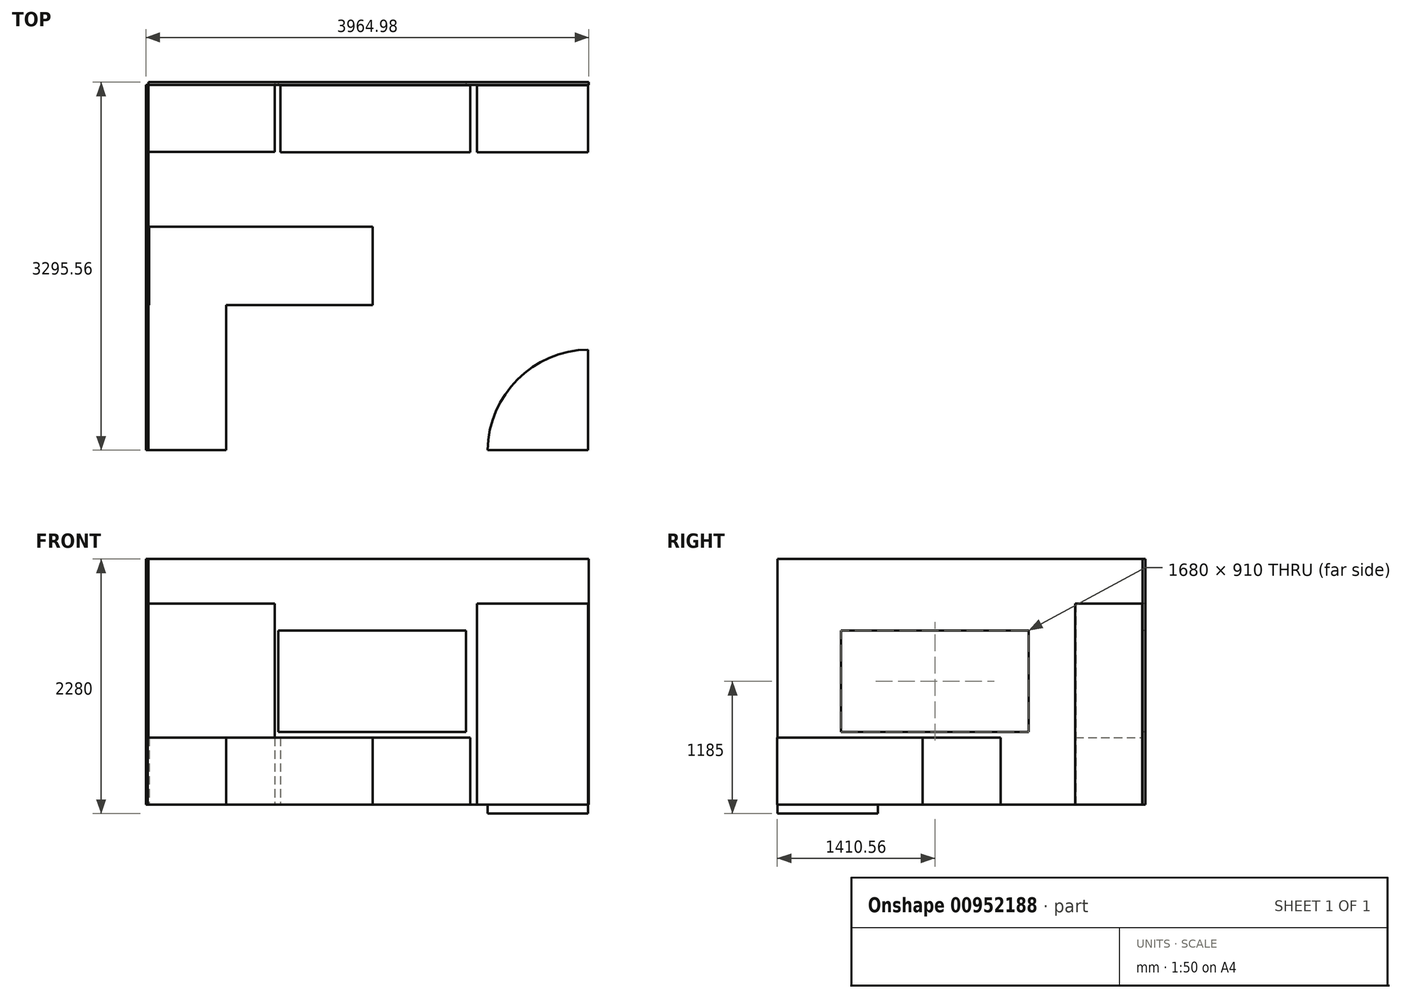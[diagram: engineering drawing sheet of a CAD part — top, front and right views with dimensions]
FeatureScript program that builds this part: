
annotation { "Feature Type Name" : "Feature", "Feature Type Description" : "" }
export const myFeature = defineFeature(function(context is Context, id is Id, definition is map)
    precondition{}
    {
        {
            var Q0;
            Q0=qCreatedBy(makeId("Top.planeOp"),FACE);
            var sketch = newSketch(context, id + "F0", { "sketchPlane" : qUnion([Q0])});
            skLineSegment(sketch, "E0.bottom", {"start": v(-2865.65, 1719.63) * mm, "end": v(1074.35, 1719.63) * mm});
            skLineSegment(sketch, "E0.top", {"start": v(-2865.65, -1550.37) * mm, "end": v(1074.35, -1550.37) * mm});
            skLineSegment(sketch, "E0.left", {"start": v(-2865.65, 1719.63) * mm, "end": v(-2865.65, -1550.37) * mm});
            skLineSegment(sketch, "E0.right", {"start": v(1074.35, 1719.63) * mm, "end": v(1074.35, -1550.37) * mm});
            skLineSegment(sketch, "E1", {"start": v(-2865.65, 699.63) * mm, "end": v(-2865.65, -980.37) * mm});
            skLineSegment(sketch, "E2", {"start": v(-1505.65, 1719.63) * mm, "end": v(174.35, 1719.63) * mm});
            skLineSegment(sketch, "E3", {"start": v(1070.5, -1539.26) * mm, "end": v(1074.35, -650.37) * mm});
            skLineSegment(sketch, "E4", {"start": v(1074.35, -650.37) * mm, "end": v(1074.35, -1550.37) * mm});
            skLineSegment(sketch, "E5", {"start": v(1074.35, -1550.37) * mm, "end": v(174.35, -1550.37) * mm});
            skArc(sketch, "E6", {"start": v(1074.35, -650.37) * mm, "mid": v(442.53, -918.55) * mm, "end": v(174.35, -1550.37) * mm});
            skSolve(sketch);
        }
        {
            var Q0;
            Q0=makeQuery(id+"F0.imprint","IMPRINT",FACE,{"disambiguationData":[TD([[makeQuery(id+"F0.imprint","IMPRINT",EDGE,{"derivedFrom":sQuery(id+"F0.wireOp",EDGE,"E0.bottom")}),-1.0]])]});
            var sketch = newSketch(context, id + "F1", { "sketchPlane" : qUnion([Q0])});
            skLineSegment(sketch, "E7.bottom", {"start": v(79.6, 1116.05) * mm, "end": v(1079.6, 1116.05) * mm});
            skLineSegment(sketch, "E7.top", {"start": v(79.6, 1716.05) * mm, "end": v(1079.6, 1716.05) * mm});
            skLineSegment(sketch, "E7.left", {"start": v(79.6, 1116.05) * mm, "end": v(79.6, 1716.05) * mm});
            skLineSegment(sketch, "E7.right", {"start": v(1079.6, 1116.05) * mm, "end": v(1079.6, 1716.05) * mm});
            skSolve(sketch);
        }
        {
            var Q0;
            Q0=makeQuery(id+"F0.imprint","IMPRINT",FACE,{"disambiguationData":[TD([[makeQuery(id+"F0.imprint","IMPRINT",EDGE,{"derivedFrom":sQuery(id+"F0.wireOp",EDGE,"E0.bottom")}),-1.0]])]});
            var sketch = newSketch(context, id + "F2", { "sketchPlane" : qUnion([Q0])});
            skLineSegment(sketch, "E8.bottom", {"start": v(-2858.85, 1719.76) * mm, "end": v(-1728.85, 1719.76) * mm});
            skLineSegment(sketch, "E8.top", {"start": v(-2858.85, 1119.76) * mm, "end": v(-1728.85, 1119.76) * mm});
            skLineSegment(sketch, "E8.left", {"start": v(-2858.85, 1719.76) * mm, "end": v(-2858.85, 1119.76) * mm});
            skLineSegment(sketch, "E8.right", {"start": v(-1728.85, 1719.76) * mm, "end": v(-1728.85, 1119.76) * mm});
            skSolve(sketch);
        }
        {
            var Q0;
            {var subQ0=sQuery(id+"F2.wireOp",EDGE,"E8.top");Q0=makeQuery(id+"F2.imprint","IMPRINT",FACE,{"disambiguationData":[TD([[makeQuery(id+"F2.imprint","IMPRINT",EDGE,{"derivedFrom":subQ0}),1.0]])]});}
            extrude(context, id + "F3", {"entities" : qUnion([Q0]), "depth" : 1800 * mm, "offsetDistance" : 25 * mm});
        }
        {
            var Q0;
            {var subQ0=sQuery(id+"F1.wireOp",EDGE,"E7.left");Q0=makeQuery(id+"F1.imprint","IMPRINT",FACE,{"disambiguationData":[TD([[makeQuery(id+"F1.imprint","IMPRINT",EDGE,{"derivedFrom":subQ0}),-1.0]])]});}
            extrude(context, id + "F4", {"entities" : qUnion([Q0]), "depth" : 1800 * mm, "offsetDistance" : 25 * mm});
        }
        {
            var Q0;
            {var subQ4=sQuery(id+"F0.wireOp",EDGE,"E0.top");Q0=makeQuery(id+"F0.imprint","IMPRINT",FACE,{"disambiguationData":[TD([[makeQuery(id+"F0.imprint","IMPRINT",EDGE,{"derivedFrom":subQ4}),1.0]])]});}
            var Q1;
            Q1=makeQuery(id+"F0.imprint","IMPRINT",FACE,{"disambiguationData":[TD([[makeQuery(id+"F0.imprint","IMPRINT",EDGE,{"derivedFrom":sQuery(id+"F0.wireOp",EDGE,"E4")}),-1.0]])]});
            extrude(context, id + "F5", {"entities" : qUnion([Q0, Q1]), "oppositeDirection" : true, "depth" : 80 * mm, "offsetDistance" : 25 * mm});
        }
        {
            var Q0;
            Q0=makeQuery(id+"F3.opExtrude","SWEPT_FACE",FACE,{"disambiguationData":[OSD([sQuery(id+"F0.wireOp",EDGE,"E0.bottom")])]});
            var sketch = newSketch(context, id + "F6", { "sketchPlane" : qUnion([Q0])});
            skLineSegment(sketch, "E9.bottom", {"start": v(18.85, 1560) * mm, "end": v(1698.85, 1560) * mm});
            skLineSegment(sketch, "E9.top", {"start": v(18.85, 650) * mm, "end": v(1698.85, 650) * mm});
            skLineSegment(sketch, "E9.left", {"start": v(18.85, 1560) * mm, "end": v(18.85, 650) * mm});
            skLineSegment(sketch, "E9.right", {"start": v(1698.85, 1560) * mm, "end": v(1698.85, 650) * mm});
            skLineSegment(sketch, "E10.bottom", {"start": v(2858.85, 0) * mm, "end": v(-1081.13, 0) * mm});
            skLineSegment(sketch, "E10.top", {"start": v(2858.85, 2200) * mm, "end": v(-1081.13, 2200) * mm});
            skLineSegment(sketch, "E10.left", {"start": v(2858.85, 0) * mm, "end": v(2858.85, 2200) * mm});
            skLineSegment(sketch, "E10.right", {"start": v(-1081.13, 0) * mm, "end": v(-1081.13, 2200) * mm});
            skLineSegment(sketch, "E11.bottom", {"start": v(190.6, 2200) * mm, "end": v(147.5, 2200) * mm});
            skSolve(sketch);
        }
        {
            var Q0;
            Q0=makeQuery(id+"F3.opExtrude","SWEPT_FACE",FACE,{"disambiguationData":[OSD([sQuery(id+"F2.wireOp",EDGE,"E8.left")])]});
            var sketch = newSketch(context, id + "F7", { "sketchPlane" : qUnion([Q0])});
            skLineSegment(sketch, "E12.bottom", {"start": v(-1719.63, 0) * mm, "end": v(1550.37, 0) * mm});
            skLineSegment(sketch, "E12.top", {"start": v(-1719.63, 2200) * mm, "end": v(1550.37, 2200) * mm});
            skLineSegment(sketch, "E12.left", {"start": v(-1719.63, 0) * mm, "end": v(-1719.63, 2200) * mm});
            skLineSegment(sketch, "E12.right", {"start": v(1550.37, 0) * mm, "end": v(1550.37, 2200) * mm});
            skLineSegment(sketch, "E13.bottom", {"start": v(-699.63, 1560) * mm, "end": v(980.37, 1560) * mm});
            skLineSegment(sketch, "E13.top", {"start": v(-699.63, 650) * mm, "end": v(980.37, 650) * mm});
            skLineSegment(sketch, "E13.left", {"start": v(-699.63, 1560) * mm, "end": v(-699.63, 650) * mm});
            skLineSegment(sketch, "E13.right", {"start": v(980.37, 1560) * mm, "end": v(980.37, 650) * mm});
            skSolve(sketch);
        }
        {
            var Q0;
            {var subQ3=sQuery(id+"F7.wireOp",EDGE,"E12.top");Q0=makeQuery(id+"F7.imprint","IMPRINT",FACE,{"disambiguationData":[TD([[makeQuery(id+"F7.imprint","IMPRINT",EDGE,{"derivedFrom":subQ3}),-1.0]])]});}
            extrude(context, id + "F8", {"entities" : qUnion([Q0]), "operationType" : NewBodyOperationType.ADD, "depth" : 25 * mm, "offsetDistance" : 25 * mm});
        }
        {
            var Q0;
            Q0=makeQuery(id+"F6.imprint","IMPRINT",FACE,{"disambiguationData":[TD([[makeQuery(id+"F6.imprint","IMPRINT",EDGE,{"derivedFrom":sQuery(id+"F6.wireOp",EDGE,"E9.bottom")}),1.0]])]});
            extrude(context, id + "F9", {"entities" : qUnion([Q0]), "depth" : 25 * mm, "offsetDistance" : 25 * mm});
        }
        {
            var Q0;
            {var subQ4=sQuery(id+"F0.wireOp",EDGE,"E0.top");Q0=makeQuery(id+"F0.imprint","IMPRINT",FACE,{"disambiguationData":[TD([[makeQuery(id+"F0.imprint","IMPRINT",EDGE,{"derivedFrom":subQ4}),1.0]])]});}
            var sketch = newSketch(context, id + "F10", { "sketchPlane" : qUnion([Q0])});
            skLineSegment(sketch, "E14.bottom", {"start": v(-2853.87, 449.07) * mm, "end": v(-853.87, 449.07) * mm});
            skLineSegment(sketch, "E14.top", {"start": v(-2853.87, -250.93) * mm, "end": v(-853.87, -250.93) * mm});
            skLineSegment(sketch, "E14.left", {"start": v(-2853.87, 449.07) * mm, "end": v(-2853.87, -250.93) * mm});
            skLineSegment(sketch, "E14.right", {"start": v(-853.87, 449.07) * mm, "end": v(-853.87, -250.93) * mm});
            skLineSegment(sketch, "E15.bottom", {"start": v(-2165.34, -250.93) * mm, "end": v(-2865.34, -250.93) * mm});
            skLineSegment(sketch, "E15.top", {"start": v(-2165.34, -1550.93) * mm, "end": v(-2865.34, -1550.93) * mm});
            skLineSegment(sketch, "E15.left", {"start": v(-2165.34, -250.93) * mm, "end": v(-2165.34, -1550.93) * mm});
            skLineSegment(sketch, "E15.right", {"start": v(-2865.34, -250.93) * mm, "end": v(-2865.34, -1550.93) * mm});
            skLineSegment(sketch, "E16.left", {"start": v(-2165.34, -1550.93) * mm, "end": v(-2151.82, -1198.55) * mm});
            skLineSegment(sketch, "E17.bottom", {"start": v(-1679.74, 1117.4) * mm, "end": v(20.26, 1117.4) * mm});
            skLineSegment(sketch, "E17.top", {"start": v(-1679.74, 1717.4) * mm, "end": v(20.26, 1717.4) * mm});
            skLineSegment(sketch, "E17.left", {"start": v(-1679.74, 1117.4) * mm, "end": v(-1679.74, 1717.4) * mm});
            skLineSegment(sketch, "E17.right", {"start": v(20.26, 1117.4) * mm, "end": v(20.26, 1717.4) * mm});
            skSolve(sketch);
        }
        {
            var Q0;
            {var subQ7=sQuery(id+"F10.wireOp",EDGE,"E17.bottom");Q0=makeQuery(id+"F10.imprint","IMPRINT",FACE,{"disambiguationData":[TD([[makeQuery(id+"F10.imprint","IMPRINT",EDGE,{"derivedFrom":subQ7}),1.0]])]});}
            extrude(context, id + "F11", {"entities" : qUnion([Q0]), "depth" : 600 * mm, "offsetDistance" : 25 * mm});
        }
        {
            var Q0;
            {var subQ1=sQuery(id+"F10.wireOp",EDGE,"E15.bottom");var subQ5=makeQuery(id+"F10.imprint","INTERSECT",VERTEX,{"derivedFrom":[sQuery(id+"F10.wireOp",EDGE,"E14.left"),subQ1]});Q0=makeQuery(id+"F10.imprint","IMPRINT",FACE,{"disambiguationData":[TD([[makeQuery(id+"F10.imprint","IMPRINT",EDGE,{"disambiguationData":[TD([[subQ5,-1.0]])],"derivedFrom":subQ1}),1.0]])]});}
            extrude(context, id + "F12", {"entities" : qUnion([Q0]), "operationType" : NewBodyOperationType.ADD, "depth" : 600 * mm, "offsetDistance" : 25 * mm});
        }
        {
            var Q0;
            Q0=makeQuery(id+"F10.imprint","IMPRINT",FACE,{"disambiguationData":[TD([[makeQuery(id+"F10.imprint","IMPRINT",EDGE,{"derivedFrom":sQuery(id+"F10.wireOp",EDGE,"E14.bottom")}),-1.0]])]});
            extrude(context, id + "F13", {"entities" : qUnion([Q0]), "operationType" : NewBodyOperationType.ADD, "depth" : 600 * mm, "offsetDistance" : 25 * mm});
        }
    });
